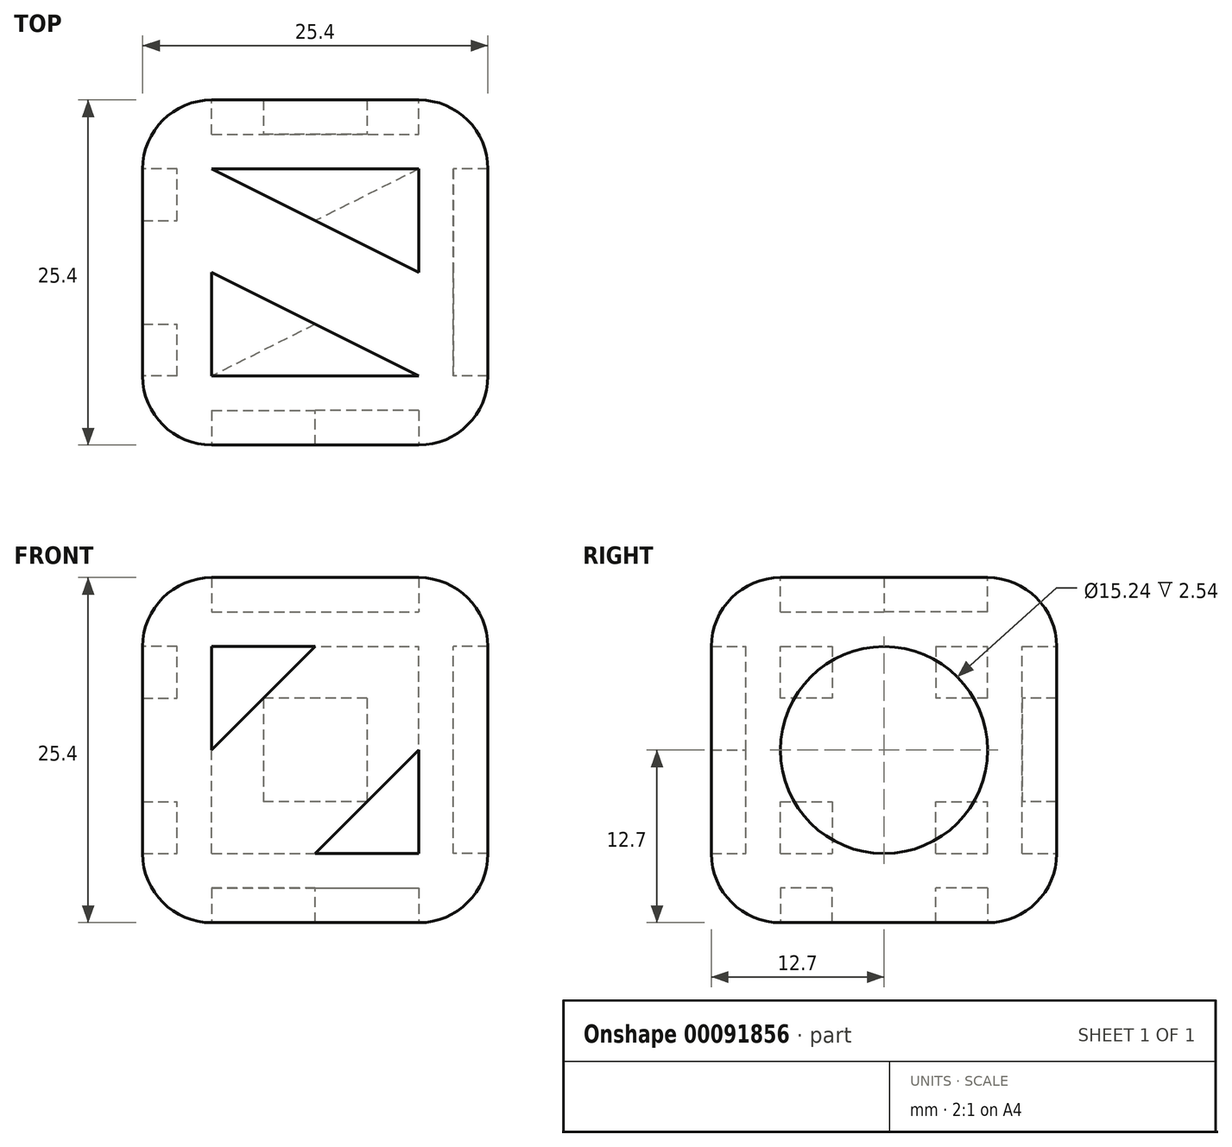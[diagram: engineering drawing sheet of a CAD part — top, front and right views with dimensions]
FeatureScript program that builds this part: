
annotation { "Feature Type Name" : "Feature", "Feature Type Description" : "" }
export const myFeature = defineFeature(function(context is Context, id is Id, definition is map)
    precondition{}
    {
        {
            var Q0;
            Q0=qCreatedBy(makeId("Front.planeOp"),FACE);
            var sketch = newSketch(context, id + "F0", { "sketchPlane" : qUnion([Q0])});
            skLineSegment(sketch, "E0.bottom", {"start": v(0, 0) * mm, "end": v(25.4, 0) * mm});
            skLineSegment(sketch, "E0.top", {"start": v(0, 25.4) * mm, "end": v(25.4, 25.4) * mm});
            skLineSegment(sketch, "E0.left", {"start": v(0, 0) * mm, "end": v(0, 25.4) * mm});
            skLineSegment(sketch, "E0.right", {"start": v(25.4, 0) * mm, "end": v(25.4, 25.4) * mm});
            skSolve(sketch);
        }
        {
            var Q0;
            Q0 = qSketchRegion(id + "F0", true);
            extrude(context, id + "F1", {"entities" : qUnion([Q0]), "depth" : 25.4 * mm});
        }
        {
            var Q0;
            Q0=makeQuery(id+"F1.opExtrude","CAP_EDGE",EDGE,{"disambiguationData":[OSD([sQuery(id+"F0.wireOp",EDGE,"E0.top")])],"isStart":false});
            var Q1;
            Q1=makeQuery(id+"F1.opExtrude","CAP_EDGE",EDGE,{"disambiguationData":[OSD([sQuery(id+"F0.wireOp",EDGE,"E0.bottom")])],"isStart":false});
            var Q2;
            Q2=makeQuery(id+"F1.opExtrude","CAP_EDGE",EDGE,{"disambiguationData":[OSD([sQuery(id+"F0.wireOp",EDGE,"E0.top")])],"isStart":true});
            var Q3;
            Q3=makeQuery(id+"F1.opExtrude","CAP_EDGE",EDGE,{"disambiguationData":[OSD([sQuery(id+"F0.wireOp",EDGE,"E0.bottom")])],"isStart":true});
            var Q4;
            Q4=makeQuery(id+"F1.opExtrude","CAP_EDGE",EDGE,{"disambiguationData":[OSD([sQuery(id+"F0.wireOp",EDGE,"E0.right")])],"isStart":true});
            var Q5;
            Q5=makeQuery(id+"F1.opExtrude","CAP_EDGE",EDGE,{"disambiguationData":[OSD([sQuery(id+"F0.wireOp",EDGE,"E0.left")])],"isStart":true});
            var Q6;
            Q6=makeQuery(id+"F1.opExtrude","SWEPT_EDGE",EDGE,{"disambiguationData":[OSD([sQuery(id+"F0.wireOp",EDGE,"E0.top"),sQuery(id+"F0.wireOp",EDGE,"E0.left")])]});
            var Q7;
            Q7=makeQuery(id+"F1.opExtrude","SWEPT_EDGE",EDGE,{"disambiguationData":[OSD([sQuery(id+"F0.wireOp",EDGE,"E0.bottom"),sQuery(id+"F0.wireOp",EDGE,"E0.left")])]});
            var Q8;
            Q8=makeQuery(id+"F1.opExtrude","SWEPT_EDGE",EDGE,{"disambiguationData":[OSD([sQuery(id+"F0.wireOp",EDGE,"E0.top"),sQuery(id+"F0.wireOp",EDGE,"E0.right")])]});
            var Q9;
            Q9=makeQuery(id+"F1.opExtrude","CAP_EDGE",EDGE,{"disambiguationData":[OSD([sQuery(id+"F0.wireOp",EDGE,"E0.right")])],"isStart":false});
            var Q10;
            Q10=makeQuery(id+"F1.opExtrude","CAP_EDGE",EDGE,{"disambiguationData":[OSD([sQuery(id+"F0.wireOp",EDGE,"E0.left")])],"isStart":false});
            var Q11;
            Q11=makeQuery(id+"F1.opExtrude","SWEPT_EDGE",EDGE,{"disambiguationData":[OSD([sQuery(id+"F0.wireOp",EDGE,"E0.bottom"),sQuery(id+"F0.wireOp",EDGE,"E0.right")])]});
            fillet(context, id + "F2", {"entities" : qUnion([Q0, Q1, Q2, Q3, Q4, Q5, Q6, Q7, Q8, Q9, Q10, Q11]), "radius" : 5.08 * mm, "tangentPropagation" : true, "allowEdgeOverflow" : false});
        }
        {
            var Q0;
            Q0=makeQuery(id+"F1.opExtrude","CAP_FACE",FACE,{"disambiguationData":[OSD([sQuery(id+"F0.wireOp",EDGE,"E0.bottom"),sQuery(id+"F0.wireOp",EDGE,"E0.top"),sQuery(id+"F0.wireOp",EDGE,"E0.left"),sQuery(id+"F0.wireOp",EDGE,"E0.right")])],"isStart":false});
            extrude(context, id + "F3", {"entities" : qUnion([Q0]), "operationType" : NewBodyOperationType.REMOVE, "oppositeDirection" : true, "depth" : 2.54 * mm});
        }
        {
            var Q0;
            Q0=makeQuery(id+"F1.opExtrude","SWEPT_FACE",FACE,{"disambiguationData":[OSD([sQuery(id+"F0.wireOp",EDGE,"E0.left")])]});
            extrude(context, id + "F4", {"entities" : qUnion([Q0]), "operationType" : NewBodyOperationType.REMOVE, "oppositeDirection" : true, "depth" : 2.54 * mm});
        }
        {
            var Q0;
            Q0=makeQuery(id+"F1.opExtrude","SWEPT_FACE",FACE,{"disambiguationData":[OSD([sQuery(id+"F0.wireOp",EDGE,"E0.top")])]});
            extrude(context, id + "F5", {"entities" : qUnion([Q0]), "operationType" : NewBodyOperationType.REMOVE, "oppositeDirection" : true, "depth" : 2.54 * mm});
        }
        {
            var Q0;
            Q0=makeQuery(id+"F1.opExtrude","SWEPT_FACE",FACE,{"disambiguationData":[OSD([sQuery(id+"F0.wireOp",EDGE,"E0.right")])]});
            extrude(context, id + "F6", {"entities" : qUnion([Q0]), "operationType" : NewBodyOperationType.REMOVE, "oppositeDirection" : true, "depth" : 2.54 * mm});
        }
        {
            var Q0;
            Q0=makeQuery(id+"F1.opExtrude","SWEPT_FACE",FACE,{"disambiguationData":[OSD([sQuery(id+"F0.wireOp",EDGE,"E0.bottom")])]});
            extrude(context, id + "F7", {"entities" : qUnion([Q0]), "operationType" : NewBodyOperationType.REMOVE, "oppositeDirection" : true, "depth" : 2.54 * mm});
        }
        {
            var Q0;
            Q0=makeQuery(id+"F1.opExtrude","CAP_FACE",FACE,{"disambiguationData":[OSD([sQuery(id+"F0.wireOp",EDGE,"E0.bottom"),sQuery(id+"F0.wireOp",EDGE,"E0.top"),sQuery(id+"F0.wireOp",EDGE,"E0.left"),sQuery(id+"F0.wireOp",EDGE,"E0.right")])],"isStart":true});
            extrude(context, id + "F8", {"entities" : qUnion([Q0]), "operationType" : NewBodyOperationType.REMOVE, "oppositeDirection" : true, "depth" : 2.54 * mm});
        }
        {
            var Q0;
            Q0=makeQuery(id+"F3.boolean.opBoolean","COPY",FACE,{"derivedFrom":makeQuery(id+"F3.opExtrude","CAP_FACE",FACE,{"disambiguationData":[OSD([sQuery(id+"F0.wireOp",EDGE,"E0.bottom"),sQuery(id+"F0.wireOp",EDGE,"E0.top"),sQuery(id+"F0.wireOp",EDGE,"E0.left"),sQuery(id+"F0.wireOp",EDGE,"E0.right")])],"isStart":false})});
            var sketch = newSketch(context, id + "F9", { "sketchPlane" : qUnion([Q0])});
            skLineSegment(sketch, "E1", {"start": v(5.08, 12.7) * mm, "end": v(12.7, 20.32) * mm});
            skLineSegment(sketch, "E2", {"start": v(12.7, 20.32) * mm, "end": v(20.32, 12.7) * mm});
            skLineSegment(sketch, "E3", {"start": v(20.32, 12.7) * mm, "end": v(12.7, 5.08) * mm});
            skLineSegment(sketch, "E4", {"start": v(12.7, 5.08) * mm, "end": v(5.08, 12.7) * mm});
            skSolve(sketch);
        }
        {
            var Q0;
            Q0=makeQuery(id+"F6.boolean.opBoolean","COPY",FACE,{"derivedFrom":makeQuery(id+"F6.opExtrude","CAP_FACE",FACE,{"disambiguationData":[OSD([sQuery(id+"F0.wireOp",EDGE,"E0.right")])],"isStart":false})});
            var sketch = newSketch(context, id + "F10", { "sketchPlane" : qUnion([Q0])});
            skCircle(sketch, "E5", {"center": v(-12.7, 12.7) * mm, "radius": 7.62 * mm});
            skPoint(sketch, "E5.centerSnap0", {"position": v(-20.32, 12.7) * mm});
            skPoint(sketch, "E5.centerSnap1", {"position": v(-12.7, 20.32) * mm});
            skSolve(sketch);
        }
        {
            var Q0;
            Q0=makeQuery(id+"F8.boolean.opBoolean","COPY",FACE,{"derivedFrom":makeQuery(id+"F8.opExtrude","CAP_FACE",FACE,{"disambiguationData":[OSD([sQuery(id+"F0.wireOp",EDGE,"E0.bottom"),sQuery(id+"F0.wireOp",EDGE,"E0.top"),sQuery(id+"F0.wireOp",EDGE,"E0.left"),sQuery(id+"F0.wireOp",EDGE,"E0.right")])],"isStart":false})});
            var sketch = newSketch(context, id + "F11", { "sketchPlane" : qUnion([Q0])});
            skPoint(sketch, "E6", {"position": v(-12.7, 20.32) * mm});
            skPoint(sketch, "E7", {"position": v(-20.32, 12.7) * mm});
            skLineSegment(sketch, "E8", {"start": v(-12.7, 20.32) * mm, "end": v(-20.32, 20.32) * mm});
            skLineSegment(sketch, "E9", {"start": v(-20.32, 20.32) * mm, "end": v(-20.32, 12.7) * mm});
            skPoint(sketch, "E10", {"position": v(-16.5, 20.32) * mm});
            skPoint(sketch, "E11", {"position": v(-20.32, 16.5) * mm});
            skLineSegment(sketch, "E12.bottom", {"start": v(-16.5, 16.5) * mm, "end": v(-8.89, 16.5) * mm});
            skLineSegment(sketch, "E12.top", {"start": v(-16.5, 8.89) * mm, "end": v(-8.89, 8.89) * mm});
            skLineSegment(sketch, "E12.left", {"start": v(-16.5, 16.5) * mm, "end": v(-16.5, 8.89) * mm});
            skLineSegment(sketch, "E12.right", {"start": v(-8.89, 16.5) * mm, "end": v(-8.89, 8.89) * mm});
            skSolve(sketch);
        }
        {
            var Q0;
            Q0=makeQuery(id+"F4.boolean.opBoolean","COPY",FACE,{"derivedFrom":makeQuery(id+"F4.opExtrude","CAP_FACE",FACE,{"disambiguationData":[OSD([sQuery(id+"F0.wireOp",EDGE,"E0.left")])],"isStart":false})});
            var sketch = newSketch(context, id + "F12", { "sketchPlane" : qUnion([Q0])});
            skPoint(sketch, "E13", {"position": v(12.7, 20.32) * mm});
            skPoint(sketch, "E14", {"position": v(5.08, 12.7) * mm});
            skPoint(sketch, "E15", {"position": v(20.32, 12.7) * mm});
            skPoint(sketch, "E16", {"position": v(12.7, 5.08) * mm});
            skLineSegment(sketch, "E17", {"start": v(12.7, 20.32) * mm, "end": v(5.08, 20.32) * mm});
            skLineSegment(sketch, "E18", {"start": v(5.08, 20.32) * mm, "end": v(5.08, 12.7) * mm});
            skPoint(sketch, "E19", {"position": v(8.9, 16.5) * mm});
            skPoint(sketch, "E19.positionSnap0", {"position": v(5.08, 16.5) * mm});
            skPoint(sketch, "E19.positionSnap1", {"position": v(8.9, 20.32) * mm});
            skLineSegment(sketch, "E20", {"start": v(5.08, 12.7) * mm, "end": v(5.08, 5.08) * mm});
            skLineSegment(sketch, "E21", {"start": v(12.7, 5.08) * mm, "end": v(20.32, 5.08) * mm});
            skLineSegment(sketch, "E22", {"start": v(20.32, 5.08) * mm, "end": v(20.32, 12.7) * mm});
            skLineSegment(sketch, "E23", {"start": v(20.32, 12.7) * mm, "end": v(20.32, 20.32) * mm});
            skLineSegment(sketch, "E24", {"start": v(20.32, 20.32) * mm, "end": v(12.7, 20.32) * mm});
            skPoint(sketch, "E25", {"position": v(16.51, 20.32) * mm});
            skPoint(sketch, "E26", {"position": v(20.32, 16.5) * mm});
            skPoint(sketch, "E27", {"position": v(20.32, 8.9) * mm});
            skPoint(sketch, "E28", {"position": v(16.51, 5.08) * mm});
            skLineSegment(sketch, "E29", {"start": v(5.08, 5.08) * mm, "end": v(12.7, 5.08) * mm});
            skPoint(sketch, "E30", {"position": v(8.9, 5.08) * mm});
            skPoint(sketch, "E31", {"position": v(5.08, 8.9) * mm});
            skLineSegment(sketch, "E32", {"start": v(8.9, 5.08) * mm, "end": v(8.9, 8.9) * mm});
            skLineSegment(sketch, "E33", {"start": v(8.9, 8.9) * mm, "end": v(5.08, 8.9) * mm});
            skLineSegment(sketch, "E34", {"start": v(5.08, 16.5) * mm, "end": v(8.9, 16.5) * mm});
            skLineSegment(sketch, "E35", {"start": v(8.9, 20.32) * mm, "end": v(8.9, 16.5) * mm});
            skLineSegment(sketch, "E36", {"start": v(16.51, 20.32) * mm, "end": v(16.51, 16.5) * mm});
            skLineSegment(sketch, "E37", {"start": v(16.51, 16.5) * mm, "end": v(20.32, 16.5) * mm});
            skLineSegment(sketch, "E38", {"start": v(20.32, 8.9) * mm, "end": v(16.51, 8.9) * mm});
            skLineSegment(sketch, "E39", {"start": v(16.51, 8.9) * mm, "end": v(16.51, 5.08) * mm});
            skSolve(sketch);
        }
        {
            var Q0;
            Q0=makeQuery(id+"F7.boolean.opBoolean","COPY",FACE,{"derivedFrom":makeQuery(id+"F7.opExtrude","CAP_FACE",FACE,{"disambiguationData":[OSD([sQuery(id+"F0.wireOp",EDGE,"E0.bottom")])],"isStart":false})});
            var sketch = newSketch(context, id + "F13", { "sketchPlane" : qUnion([Q0])});
            skLineSegment(sketch, "E40", {"start": v(20.32, 5.08) * mm, "end": v(5.08, 12.7) * mm});
            skLineSegment(sketch, "E41", {"start": v(5.08, 12.7) * mm, "end": v(20.32, 20.32) * mm});
            skPoint(sketch, "E42", {"position": v(12.7, 8.9) * mm});
            skPoint(sketch, "E43", {"position": v(12.7, 16.51) * mm});
            skLineSegment(sketch, "E44", {"start": v(5.08, 5.08) * mm, "end": v(12.7, 8.9) * mm});
            skLineSegment(sketch, "E45", {"start": v(12.7, 16.51) * mm, "end": v(5.08, 20.32) * mm});
            skSolve(sketch);
        }
        {
            var Q0;
            Q0=makeQuery(id+"F5.boolean.opBoolean","COPY",FACE,{"derivedFrom":makeQuery(id+"F5.opExtrude","CAP_FACE",FACE,{"disambiguationData":[OSD([sQuery(id+"F0.wireOp",EDGE,"E0.top")])],"isStart":false})});
            var sketch = newSketch(context, id + "F14", { "sketchPlane" : qUnion([Q0])});
            skPoint(sketch, "E46", {"position": v(20.32, -12.7) * mm});
            skPoint(sketch, "E47", {"position": v(5.08, -12.7) * mm});
            skLineSegment(sketch, "E48", {"start": v(20.32, -12.7) * mm, "end": v(20.32, -20.32) * mm});
            skLineSegment(sketch, "E49", {"start": v(20.32, -20.32) * mm, "end": v(5.08, -12.7) * mm});
            skLineSegment(sketch, "E50", {"start": v(5.08, -5.08) * mm, "end": v(20.32, -12.7) * mm});
            skSolve(sketch);
        }
        {
            var Q0;
            Q0=makeQuery(id+"F14.imprint","IMPRINT",FACE,{"disambiguationData":[TD([[makeQuery(id+"F14.imprint","IMPRINT",EDGE,{"derivedFrom":sQuery(id+"F14.wireOp",EDGE,"E48")}),1.0]])]});
            extrude(context, id + "F15", {"entities" : qUnion([Q0]), "operationType" : NewBodyOperationType.ADD, "depth" : 2.54 * mm});
        }
        {
            var Q0;
            Q0=makeQuery(id+"F11.imprint","IMPRINT",FACE,{"disambiguationData":[TD([[makeQuery(id+"F11.imprint","IMPRINT",EDGE,{"derivedFrom":sQuery(id+"F11.wireOp",EDGE,"E12.bottom")}),-1.0]])]});
            extrude(context, id + "F16", {"entities" : qUnion([Q0]), "operationType" : NewBodyOperationType.ADD, "depth" : 2.54 * mm});
        }
        {
            var Q0;
            {var subQ0=sQuery(id+"F9.wireOp",EDGE,"E4");Q0=makeQuery(id+"F9.imprint","IMPRINT",FACE,{"disambiguationData":[TD([[makeQuery(id+"F9.imprint","IMPRINT",EDGE,{"derivedFrom":subQ0}),1.0]])]});}
            var Q1;
            Q1=makeQuery(id+"F9.imprint","IMPRINT",FACE,{"disambiguationData":[TD([[makeQuery(id+"F9.imprint","IMPRINT",EDGE,{"derivedFrom":sQuery(id+"F9.wireOp",EDGE,"E1")}),-1.0]])]});
            var Q2;
            {var subQ0=sQuery(id+"F9.wireOp",EDGE,"E2");Q2=makeQuery(id+"F9.imprint","IMPRINT",FACE,{"disambiguationData":[TD([[makeQuery(id+"F9.imprint","IMPRINT",EDGE,{"derivedFrom":subQ0}),1.0]])]});}
            extrude(context, id + "F17", {"entities" : qUnion([Q0, Q1, Q2]), "operationType" : NewBodyOperationType.ADD, "depth" : 2.54 * mm});
        }
        {
            var Q0;
            {var subQ0=sQuery(id+"F12.wireOp",EDGE,"E32");Q0=makeQuery(id+"F12.imprint","IMPRINT",FACE,{"disambiguationData":[TD([[makeQuery(id+"F12.imprint","IMPRINT",EDGE,{"derivedFrom":subQ0}),-1.0]])]});}
            extrude(context, id + "F18", {"entities" : qUnion([Q0]), "operationType" : NewBodyOperationType.ADD, "depth" : 2.54 * mm});
        }
        {
            var Q0;
            {var subQ1=sQuery(id+"F0.wireOp",EDGE,"E0.bottom");var subQ3=makeQuery(id+"F7.boolean.opBoolean","COPY",EDGE,{"derivedFrom":makeQuery(id+"F7.opExtrude","CAP_EDGE",EDGE,{"disambiguationData":[OSD([subQ1,sQuery(id+"F0.wireOp",EDGE,"E0.right")])],"isStart":false})});Q0=makeQuery(id+"F13.imprint","IMPRINT",FACE,{"disambiguationData":[TD([[makeQuery(id+"F13.imprint","IMPRINT",EDGE,{"derivedFrom":subQ3}),1.0]])]});}
            var Q1;
            {var subQ4=sQuery(id+"F13.wireOp",EDGE,"E44");Q1=makeQuery(id+"F13.imprint","IMPRINT",FACE,{"disambiguationData":[TD([[makeQuery(id+"F13.imprint","IMPRINT",EDGE,{"derivedFrom":subQ4}),1.0]])]});}
            var Q2;
            {var subQ4=sQuery(id+"F13.wireOp",EDGE,"E45");Q2=makeQuery(id+"F13.imprint","IMPRINT",FACE,{"disambiguationData":[TD([[makeQuery(id+"F13.imprint","IMPRINT",EDGE,{"derivedFrom":subQ4}),1.0]])]});}
            extrude(context, id + "F19", {"entities" : qUnion([Q0, Q1, Q2]), "operationType" : NewBodyOperationType.ADD, "depth" : 2.54 * mm});
        }
        {
            var Q0;
            {var subQ0=sQuery(id+"F10.wireOp",EDGE,"E5");var subQ1=sQuery(id+"F0.wireOp",EDGE,"E0.right");var subQ2=makeQuery(id+"F6.boolean.opBoolean","COPY",EDGE,{"derivedFrom":makeQuery(id+"F6.opExtrude","CAP_EDGE",EDGE,{"disambiguationData":[OSD([subQ1]),TDD([makeQuery(id+"F2.opFillet","BLEND_EDGE",EDGE,{"blendedFrom":[makeQuery(id+"F1.opExtrude","CAP_EDGE",EDGE,{"disambiguationData":[OSD([subQ1])],"isStart":true}),makeQuery(id+"F1.opExtrude","SWEPT_FACE",FACE,{"disambiguationData":[OSD([subQ1])]})],"blendedInto":[makeQuery(id+"F1.opExtrude","SWEPT_FACE",FACE,{"disambiguationData":[OSD([subQ1])]})]})])],"isStart":false})});var subQ3=makeQuery(id+"F10.imprint","INTERSECT",VERTEX,{"derivedFrom":[subQ2,subQ0]});Q0=makeQuery(id+"F10.imprint","IMPRINT",FACE,{"disambiguationData":[TD([[makeQuery(id+"F10.imprint","IMPRINT",EDGE,{"disambiguationData":[TD([[subQ3,1.0]])],"derivedFrom":subQ0}),-1.0]])]});}
            var Q1;
            {var subQ0=sQuery(id+"F10.wireOp",EDGE,"E5");var subQ1=sQuery(id+"F0.wireOp",EDGE,"E0.right");var subQ2=makeQuery(id+"F6.boolean.opBoolean","COPY",EDGE,{"derivedFrom":makeQuery(id+"F6.opExtrude","CAP_EDGE",EDGE,{"disambiguationData":[OSD([subQ1]),TDD([makeQuery(id+"F2.opFillet","BLEND_EDGE",EDGE,{"blendedFrom":[makeQuery(id+"F1.opExtrude","CAP_EDGE",EDGE,{"disambiguationData":[OSD([subQ1])],"isStart":false}),makeQuery(id+"F1.opExtrude","SWEPT_FACE",FACE,{"disambiguationData":[OSD([subQ1])]})],"blendedInto":[makeQuery(id+"F1.opExtrude","SWEPT_FACE",FACE,{"disambiguationData":[OSD([subQ1])]})]})])],"isStart":false})});var subQ3=makeQuery(id+"F10.imprint","INTERSECT",VERTEX,{"derivedFrom":[subQ2,subQ0]});Q1=makeQuery(id+"F10.imprint","IMPRINT",FACE,{"disambiguationData":[TD([[makeQuery(id+"F10.imprint","IMPRINT",EDGE,{"disambiguationData":[TD([[subQ3,-1.0]])],"derivedFrom":subQ0}),-1.0]])]});}
            var Q2;
            {var subQ0=sQuery(id+"F10.wireOp",EDGE,"E5");var subQ1=sQuery(id+"F0.wireOp",EDGE,"E0.right");var subQ4=makeQuery(id+"F6.boolean.opBoolean","COPY",EDGE,{"derivedFrom":makeQuery(id+"F6.opExtrude","CAP_EDGE",EDGE,{"disambiguationData":[OSD([subQ1]),TDD([makeQuery(id+"F2.opFillet","BLEND_EDGE",EDGE,{"blendedFrom":[makeQuery(id+"F1.opExtrude","CAP_EDGE",EDGE,{"disambiguationData":[OSD([subQ1])],"isStart":true}),makeQuery(id+"F1.opExtrude","SWEPT_FACE",FACE,{"disambiguationData":[OSD([subQ1])]})],"blendedInto":[makeQuery(id+"F1.opExtrude","SWEPT_FACE",FACE,{"disambiguationData":[OSD([subQ1])]})]})])],"isStart":false})});var subQ5=makeQuery(id+"F10.imprint","INTERSECT",VERTEX,{"derivedFrom":[subQ4,subQ0]});Q2=makeQuery(id+"F10.imprint","IMPRINT",FACE,{"disambiguationData":[TD([[makeQuery(id+"F10.imprint","IMPRINT",EDGE,{"disambiguationData":[TD([[subQ5,-1.0]])],"derivedFrom":subQ0}),-1.0]])]});}
            var Q3;
            {var subQ0=sQuery(id+"F10.wireOp",EDGE,"E5");var subQ1=sQuery(id+"F0.wireOp",EDGE,"E0.right");var subQ4=makeQuery(id+"F6.boolean.opBoolean","COPY",EDGE,{"derivedFrom":makeQuery(id+"F6.opExtrude","CAP_EDGE",EDGE,{"disambiguationData":[OSD([subQ1]),TDD([makeQuery(id+"F2.opFillet","BLEND_EDGE",EDGE,{"blendedFrom":[makeQuery(id+"F1.opExtrude","CAP_EDGE",EDGE,{"disambiguationData":[OSD([subQ1])],"isStart":false}),makeQuery(id+"F1.opExtrude","SWEPT_FACE",FACE,{"disambiguationData":[OSD([subQ1])]})],"blendedInto":[makeQuery(id+"F1.opExtrude","SWEPT_FACE",FACE,{"disambiguationData":[OSD([subQ1])]})]})])],"isStart":false})});var subQ5=makeQuery(id+"F10.imprint","INTERSECT",VERTEX,{"derivedFrom":[subQ4,subQ0]});Q3=makeQuery(id+"F10.imprint","IMPRINT",FACE,{"disambiguationData":[TD([[makeQuery(id+"F10.imprint","IMPRINT",EDGE,{"disambiguationData":[TD([[subQ5,1.0]])],"derivedFrom":subQ0}),-1.0]])]});}
            extrude(context, id + "F20", {"entities" : qUnion([Q0, Q1, Q2, Q3]), "operationType" : NewBodyOperationType.ADD, "depth" : 2.54 * mm});
        }
    });
